# Revit family: NICE XL
name_source: partatom
category: Lighting Fixtures
units: mm (PartAtom-declared; Revit-internal decimal feet)

## family parameters
Cut with Voids When Loaded = No
Host = Face
Light Source = Yes
Maintain Annotation Orientation = Yes
Part Type = Normal
Room Calculation Point = No
Round Connector Dimension = Use Diameter
Shared = No

## types (6) — shared parameters
Color Filter = 16777215
Default Elevation = 1219 mm
Dimming Lamp Color Temperature Shift = <None>
Emit from Line Length = 610 mm
LuxLight_Amperios = 350
LuxLight_Lumenes = 1050 lm
LuxLight_Temperatura = 2700 K
Manufacturer = LUXLIGHT
Tilt Angle = 0.00°
zero-valued in all types: LuxLight_Alto, LuxLight_AltoAreaLuminosa, LuxLight_Ancho, LuxLight_AnchoAreaLuminosa, LuxLight_Diametro, LuxLight_DiametroAreaLuminosa, LuxLight_Largo, LuxLight_LargoAreaLuminosa, LuxLight_ProtuberanciaTecho

## per-type parameters (varying)
| type | LuxLight_Watios | Photometric Web File |
| LXRNIXLR992x | 9 W | LXRNIXLR9921 .ies |
| LXRNIXLR993x | 9 W | LXRNIXLR9931 .ies |
| LXRNIXLR994x | 9 W | LXRNIXLR9941 .ies |
| LXRNIXLR92x | 12 W | LXRNIXLR921 .ies |
| LXRNIXLR93x | 12 W | LXRNIXLR931 .ies |
| LXRNIXLR94x | 12 W | LXRNIXLR941 .ies |

## geometry (parser evidence)
native form markers: Sweep x2
no freeform markers — native parametric forms only
